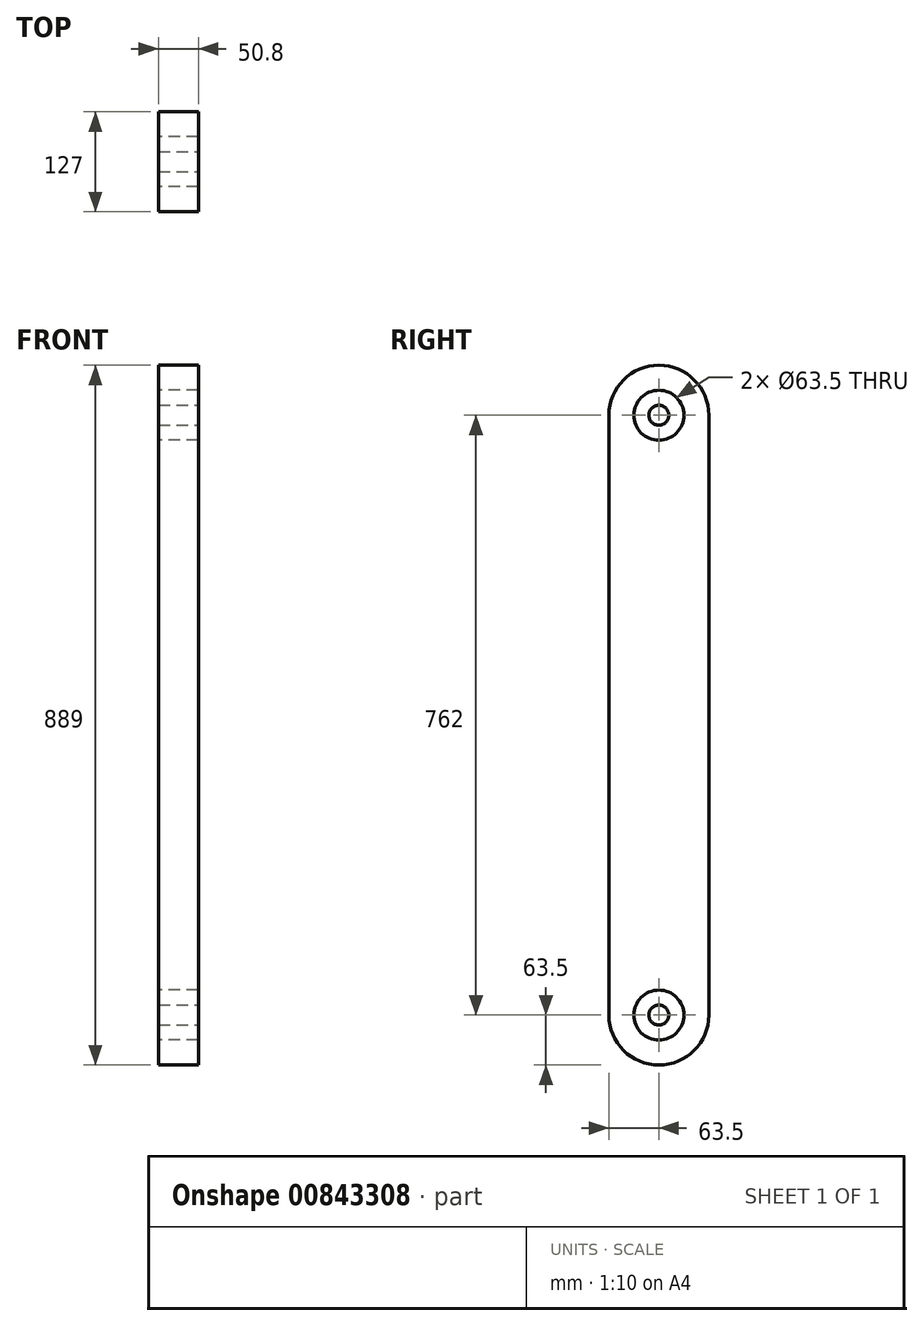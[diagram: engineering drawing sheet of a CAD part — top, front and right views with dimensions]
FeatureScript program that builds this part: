
annotation { "Feature Type Name" : "Feature", "Feature Type Description" : "" }
export const myFeature = defineFeature(function(context is Context, id is Id, definition is map)
    precondition{}
    {
        {
            var Q0;
            Q0=qCreatedBy(makeId("Right.planeOp"),FACE);
            var sketch = newSketch(context, id + "F0", { "sketchPlane" : qUnion([Q0])});
            skLineSegment(sketch, "E0.left", {"start": v(0, 0) * mm, "end": v(0, 762) * mm});
            skLineSegment(sketch, "E0.right", {"start": v(127, 0) * mm, "end": v(127, 762) * mm});
            skArc(sketch, "E1", {"start": v(127, 762) * mm, "mid": v(63.5, 825.5) * mm, "end": v(0, 762) * mm});
            skArc(sketch, "E2", {"start": v(0, 0) * mm, "mid": v(63.5, -63.5) * mm, "end": v(127, 0) * mm});
            skCircle(sketch, "E3", {"center": v(63.5, 762) * mm, "radius": 31.75 * mm});
            skCircle(sketch, "E4", {"center": v(63.5, 0) * mm, "radius": 31.75 * mm});
            skSolve(sketch);
        }
        {
            var Q0;
            Q0=makeQuery(id+"F0.imprint","IMPRINT",FACE,{"disambiguationData":[TD([[makeQuery(id+"F0.imprint","IMPRINT",EDGE,{"derivedFrom":sQuery(id+"F0.wireOp",EDGE,"E0.left")}),-1.0]])]});
            extrude(context, id + "F1", {"entities" : qUnion([Q0]), "depth" : 50.8 * mm, "offsetDistance" : 25.4 * mm});
        }
        {
            var Q0;
            Q0=makeQuery(id+"F1.opExtrude","CAP_FACE",FACE,{"disambiguationData":[OSD([sQuery(id+"F0.wireOp",EDGE,"E0.left"),sQuery(id+"F0.wireOp",EDGE,"E0.right"),sQuery(id+"F0.wireOp",EDGE,"E1"),sQuery(id+"F0.wireOp",EDGE,"E2"),sQuery(id+"F0.wireOp",EDGE,"E3"),sQuery(id+"F0.wireOp",EDGE,"E4")])],"isStart":false});
            var sketch = newSketch(context, id + "F2", { "sketchPlane" : qUnion([Q0])});
            skCircle(sketch, "E5", {"center": v(63.5, 762) * mm, "radius": 12.7 * mm});
            skCircle(sketch, "E6", {"center": v(63.5, 0) * mm, "radius": 12.7 * mm});
            skSolve(sketch);
        }
        {
            var Q0;
            Q0 = qSketchRegion(id + "F2", true);
            extrude(context, id + "F3", {"entities" : qUnion([Q0]), "oppositeDirection" : true, "depth" : 50.8 * mm, "offsetDistance" : 25.4 * mm});
        }
    });
